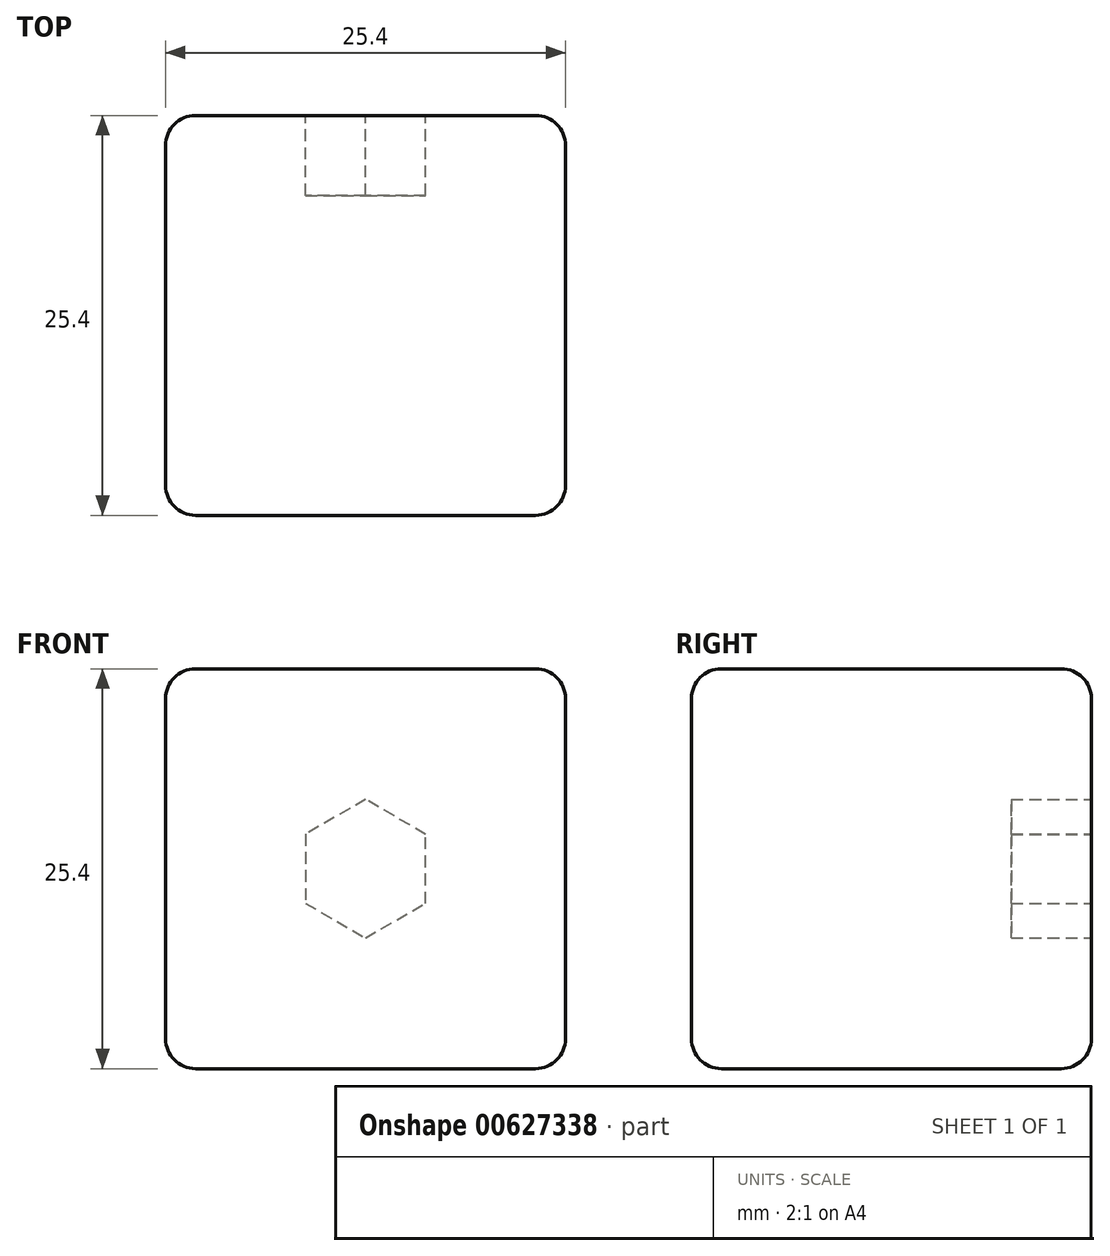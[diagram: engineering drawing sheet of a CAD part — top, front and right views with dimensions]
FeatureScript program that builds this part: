
annotation { "Feature Type Name" : "Feature", "Feature Type Description" : "" }
export const myFeature = defineFeature(function(context is Context, id is Id, definition is map)
    precondition{}
    {
        {
            var Q0;
            Q0=qCreatedBy(makeId("Top.planeOp"),FACE);
            var sketch = newSketch(context, id + "F0", { "sketchPlane" : qUnion([Q0])});
            skLineSegment(sketch, "E0", {"start": v(-12.7, 12.86) * mm, "end": v(12.7, 12.86) * mm});
            skLineSegment(sketch, "E1", {"start": v(12.7, 12.86) * mm, "end": v(12.7, -12.54) * mm});
            skLineSegment(sketch, "E2", {"start": v(12.7, -12.54) * mm, "end": v(-12.7, -12.54) * mm});
            skLineSegment(sketch, "E3", {"start": v(-12.7, 12.86) * mm, "end": v(-12.7, -12.54) * mm});
            skSolve(sketch);
        }
        {
            var Q0;
            Q0=makeQuery(id+"F0.imprint","IMPRINT",FACE,{"disambiguationData":[TD([[makeQuery(id+"F0.imprint","IMPRINT",EDGE,{"derivedFrom":sQuery(id+"F0.wireOp",EDGE,"E0")}),-1.0]])]});
            extrude(context, id + "F1", {"entities" : qUnion([Q0]), "depth" : 25.4 * mm, "offsetDistance" : 25.4 * mm});
        }
        {
            var Q0;
            Q0=makeQuery(id+"F1.opExtrude","CAP_FACE",FACE,{"disambiguationData":[OSD([sQuery(id+"F0.wireOp",EDGE,"E0"),sQuery(id+"F0.wireOp",EDGE,"E1"),sQuery(id+"F0.wireOp",EDGE,"E2"),sQuery(id+"F0.wireOp",EDGE,"E3")])],"isStart":false});
            var Q1;
            Q1=makeQuery(id+"F1.opExtrude","SWEPT_FACE",FACE,{"disambiguationData":[OSD([sQuery(id+"F0.wireOp",EDGE,"E1")])]});
            var Q2;
            Q2=makeQuery(id+"F1.opExtrude","SWEPT_FACE",FACE,{"disambiguationData":[OSD([sQuery(id+"F0.wireOp",EDGE,"E2")])]});
            var Q3;
            Q3=makeQuery(id+"F1.opExtrude","SWEPT_FACE",FACE,{"disambiguationData":[OSD([sQuery(id+"F0.wireOp",EDGE,"E0")])]});
            var Q4;
            Q4=makeQuery(id+"F1.opExtrude","SWEPT_FACE",FACE,{"disambiguationData":[OSD([sQuery(id+"F0.wireOp",EDGE,"E3")])]});
            var Q5;
            Q5=makeQuery(id+"F1.opExtrude","CAP_FACE",FACE,{"disambiguationData":[OSD([sQuery(id+"F0.wireOp",EDGE,"E0"),sQuery(id+"F0.wireOp",EDGE,"E1"),sQuery(id+"F0.wireOp",EDGE,"E2"),sQuery(id+"F0.wireOp",EDGE,"E3")])],"isStart":true});
            fillet(context, id + "F2", {"entities" : qUnion([Q0, Q1, Q2, Q3, Q4, Q5]), "radius" : 1.9 * mm, "tangentPropagation" : true, "allowEdgeOverflow" : false});
        }
        {
            var Q0;
            Q0=makeQuery(id+"F1.opExtrude","SWEPT_FACE",FACE,{"disambiguationData":[OSD([sQuery(id+"F0.wireOp",EDGE,"E0")])]});
            var sketch = newSketch(context, id + "F3", { "sketchPlane" : qUnion([Q0])});
            skCircle(sketch, "E4.cCircle", {"center": v(0, 12.7) * mm, "radius": 3.81 * mm, "construction": true});
            skPoint(sketch, "E4.cCircle.centerSnap0", {"position": v(10.8, 12.7) * mm});
            skLineSegment(sketch, "E4.0", {"start": v(3.81, 10.5) * mm, "end": v(0, 8.3) * mm});
            skLineSegment(sketch, "E4.1", {"start": v(0, 8.3) * mm, "end": v(-3.8, 10.5) * mm});
            skLineSegment(sketch, "E4.2", {"start": v(-3.8, 10.5) * mm, "end": v(-3.81, 14.9) * mm});
            skLineSegment(sketch, "E4.3", {"start": v(-3.81, 14.9) * mm, "end": v(0, 17.1) * mm});
            skLineSegment(sketch, "E4.4", {"start": v(0, 17.1) * mm, "end": v(3.8, 14.9) * mm});
            skLineSegment(sketch, "E4.5", {"start": v(3.8, 14.9) * mm, "end": v(3.81, 10.5) * mm});
            skPoint(sketch, "E4.0.midPoint", {"position": v(1.91, 9.4) * mm});
            skSolve(sketch);
        }
        {
            var Q0;
            Q0 = qSketchRegion(id + "F3", true);
            extrude(context, id + "F4", {"entities" : qUnion([Q0]), "operationType" : NewBodyOperationType.REMOVE, "oppositeDirection" : true, "depth" : 5.08 * mm, "offsetDistance" : 25.4 * mm});
        }
    });
